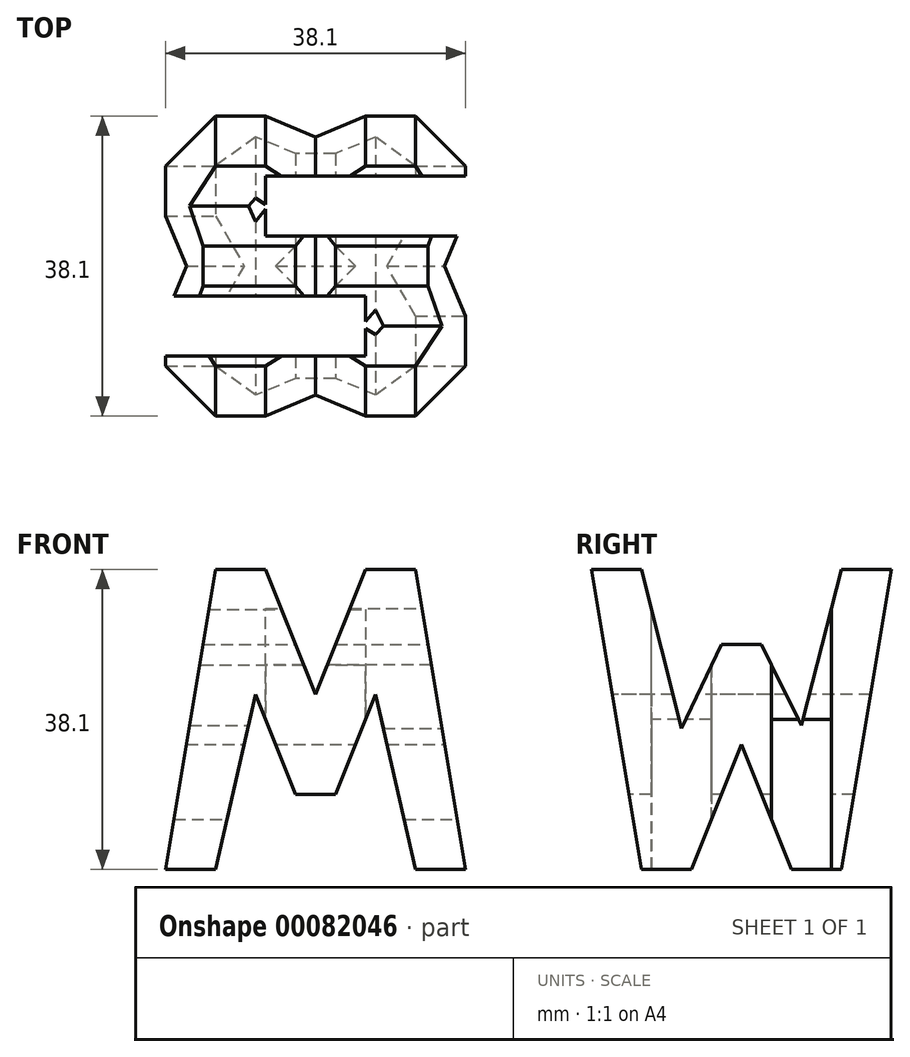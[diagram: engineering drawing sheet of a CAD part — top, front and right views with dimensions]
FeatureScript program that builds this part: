
annotation { "Feature Type Name" : "Feature", "Feature Type Description" : "" }
export const myFeature = defineFeature(function(context is Context, id is Id, definition is map)
    precondition{}
    {
        {
            var Q0;
            Q0=qCreatedBy(makeId("Front.planeOp"),FACE);
            var sketch = newSketch(context, id + "F0", { "sketchPlane" : qUnion([Q0])});
            skLineSegment(sketch, "E0", {"start": v(0, 0) * mm, "end": v(0, 38.1) * mm});
            skLineSegment(sketch, "E1", {"start": v(0, 38.1) * mm, "end": v(38.1, 38.1) * mm});
            skLineSegment(sketch, "E2", {"start": v(38.1, 38.1) * mm, "end": v(38.1, 0) * mm});
            skLineSegment(sketch, "E3", {"start": v(38.1, 0) * mm, "end": v(0, 0) * mm});
            skSolve(sketch);
        }
        {
            var Q0;
            Q0=makeQuery(id+"F0.imprint","IMPRINT",FACE,{"disambiguationData":[TD([[makeQuery(id+"F0.imprint","IMPRINT",EDGE,{"derivedFrom":sQuery(id+"F0.wireOp",EDGE,"E0")}),-1.0]])]});
            extrude(context, id + "F1", {"entities" : qUnion([Q0]), "depth" : 38.1 * mm});
        }
        {
            var Q0;
            Q0=qCreatedBy(makeId("Front.planeOp"),FACE);
            cPlane(context, id + "F2", {"entities" : qUnion([Q0]), "cplaneType" : CPlaneType.OFFSET, "offset" : 38.1 * mm, "width" : 152.4 * mm, "height" : 152.4 * mm});
        }
        {
            var Q0;
            Q0=qCreatedBy(makeId("Right.planeOp"),FACE);
            cPlane(context, id + "F3", {"entities" : qUnion([Q0]), "cplaneType" : CPlaneType.OFFSET, "offset" : 38.1 * mm, "width" : 152.4 * mm, "height" : 152.4 * mm});
        }
        {
            var Q0;
            Q0=qCreatedBy(makeId("Top.planeOp"),FACE);
            cPlane(context, id + "F4", {"entities" : qUnion([Q0]), "cplaneType" : CPlaneType.OFFSET, "offset" : 38.1 * mm, "width" : 152.4 * mm, "height" : 152.4 * mm});
        }
        {
            var Q0;
            Q0=qCreatedBy(id+"F3.planeOp",FACE);
            var sketch = newSketch(context, id + "F5", { "sketchPlane" : qUnion([Q0])});
            skLineSegment(sketch, "E4", {"start": v(0, 0) * mm, "end": v(-38.1, 0) * mm});
            skLineSegment(sketch, "E5", {"start": v(-38.1, 0) * mm, "end": v(-38.1, 38.1) * mm});
            skLineSegment(sketch, "E6", {"start": v(-38.1, 38.1) * mm, "end": v(0, 38.1) * mm});
            skLineSegment(sketch, "E7", {"start": v(0, 38.1) * mm, "end": v(0, 0) * mm});
            skLineSegment(sketch, "E8", {"start": v(-38.1, 38.1) * mm, "end": v(-31.75, 0) * mm});
            skLineSegment(sketch, "E9", {"start": v(-31.75, 38.1) * mm, "end": v(-26.67, 17.88) * mm});
            skLineSegment(sketch, "E10", {"start": v(-26.67, 17.88) * mm, "end": v(-21.59, 28.58) * mm});
            skLineSegment(sketch, "E11", {"start": v(-21.6, 28.58) * mm, "end": v(-16.51, 28.58) * mm});
            skLineSegment(sketch, "E12", {"start": v(-16.51, 28.58) * mm, "end": v(-11.43, 18.3) * mm});
            skLineSegment(sketch, "E13", {"start": v(-11.43, 18.3) * mm, "end": v(-6.35, 38.1) * mm});
            skLineSegment(sketch, "E14", {"start": v(-6.35, 38.1) * mm, "end": v(0, 38.1) * mm});
            skLineSegment(sketch, "E15", {"start": v(0, 38.1) * mm, "end": v(-6.35, 0) * mm});
            skLineSegment(sketch, "E16", {"start": v(-12.7, 0) * mm, "end": v(-19.05, 15.88) * mm});
            skLineSegment(sketch, "E17", {"start": v(-19.05, 15.88) * mm, "end": v(-25.4, 0) * mm});
            skSolve(sketch);
        }
        {
            var Q0;
            {var subQ0=sQuery(id+"F5.wireOp",EDGE,"E9");Q0=makeQuery(id+"F5.imprint","IMPRINT",FACE,{"disambiguationData":[TD([[makeQuery(id+"F5.imprint","IMPRINT",EDGE,{"derivedFrom":subQ0}),1.0]])]});}
            var Q1;
            {var subQ0=sQuery(id+"F5.wireOp",EDGE,"E5");Q1=makeQuery(id+"F5.imprint","IMPRINT",FACE,{"disambiguationData":[TD([[makeQuery(id+"F5.imprint","IMPRINT",EDGE,{"derivedFrom":subQ0}),-1.0]])]});}
            var Q2;
            {var subQ0=sQuery(id+"F5.wireOp",EDGE,"E16");Q2=makeQuery(id+"F5.imprint","IMPRINT",FACE,{"disambiguationData":[TD([[makeQuery(id+"F5.imprint","IMPRINT",EDGE,{"derivedFrom":subQ0}),1.0]])]});}
            var Q3;
            {var subQ0=sQuery(id+"F5.wireOp",EDGE,"E7");Q3=makeQuery(id+"F5.imprint","IMPRINT",FACE,{"disambiguationData":[TD([[makeQuery(id+"F5.imprint","IMPRINT",EDGE,{"derivedFrom":subQ0}),-1.0]])]});}
            extrude(context, id + "F6", {"entities" : qUnion([Q0, Q1, Q2, Q3]), "operationType" : NewBodyOperationType.REMOVE, "oppositeDirection" : true, "depth" : 38.1 * mm});
        }
        {
            var Q0;
            Q0=qCreatedBy(id+"F2.planeOp",FACE);
            var sketch = newSketch(context, id + "F7", { "sketchPlane" : qUnion([Q0])});
            skLineSegment(sketch, "E18", {"start": v(0, 0) * mm, "end": v(0, 38.1) * mm});
            skLineSegment(sketch, "E19", {"start": v(0, 38.1) * mm, "end": v(38.1, 38.1) * mm});
            skLineSegment(sketch, "E20", {"start": v(38.1, 38.1) * mm, "end": v(38.1, 0) * mm});
            skLineSegment(sketch, "E21", {"start": v(38.1, 0) * mm, "end": v(0, 0) * mm});
            skLineSegment(sketch, "E22", {"start": v(0, 0) * mm, "end": v(6.35, 38.1) * mm});
            skLineSegment(sketch, "E23", {"start": v(12.7, 38.1) * mm, "end": v(19.05, 22.22) * mm});
            skLineSegment(sketch, "E24", {"start": v(19.05, 22.22) * mm, "end": v(25.4, 38.1) * mm});
            skLineSegment(sketch, "E25", {"start": v(31.75, 38.1) * mm, "end": v(38.1, 0) * mm});
            skLineSegment(sketch, "E26", {"start": v(38.1, 0) * mm, "end": v(31.75, 0) * mm});
            skLineSegment(sketch, "E27", {"start": v(31.75, 0) * mm, "end": v(26.67, 22.22) * mm});
            skLineSegment(sketch, "E28", {"start": v(26.67, 22.22) * mm, "end": v(21.6, 9.53) * mm});
            skLineSegment(sketch, "E29", {"start": v(21.59, 9.52) * mm, "end": v(16.51, 9.52) * mm});
            skLineSegment(sketch, "E30", {"start": v(16.51, 9.52) * mm, "end": v(11.43, 22.23) * mm});
            skLineSegment(sketch, "E31", {"start": v(11.43, 22.23) * mm, "end": v(6.35, 0) * mm});
            skSolve(sketch);
        }
        {
            var Q0;
            {var subQ0=sQuery(id+"F7.wireOp",EDGE,"E23");Q0=makeQuery(id+"F7.imprint","IMPRINT",FACE,{"disambiguationData":[TD([[makeQuery(id+"F7.imprint","IMPRINT",EDGE,{"derivedFrom":subQ0}),1.0]])]});}
            var sketch = newSketch(context, id + "F8", { "sketchPlane" : qUnion([Q0])});
            skSolve(sketch);
        }
        {
            var Q0;
            Q0 = qSketchRegion(id + "F8", true);
            var Q1;
            {var subQ0=sQuery(id+"F7.wireOp",EDGE,"E23");Q1=makeQuery(id+"F7.imprint","IMPRINT",FACE,{"disambiguationData":[TD([[makeQuery(id+"F7.imprint","IMPRINT",EDGE,{"derivedFrom":subQ0}),1.0]])]});}
            var Q2;
            {var subQ0=sQuery(id+"F7.wireOp",EDGE,"E18");Q2=makeQuery(id+"F7.imprint","IMPRINT",FACE,{"disambiguationData":[TD([[makeQuery(id+"F7.imprint","IMPRINT",EDGE,{"derivedFrom":subQ0}),-1.0]])]});}
            var Q3;
            {var subQ0=sQuery(id+"F7.wireOp",EDGE,"E27");Q3=makeQuery(id+"F7.imprint","IMPRINT",FACE,{"disambiguationData":[TD([[makeQuery(id+"F7.imprint","IMPRINT",EDGE,{"derivedFrom":subQ0}),1.0]])]});}
            var Q4;
            {var subQ0=sQuery(id+"F7.wireOp",EDGE,"E20");Q4=makeQuery(id+"F7.imprint","IMPRINT",FACE,{"disambiguationData":[TD([[makeQuery(id+"F7.imprint","IMPRINT",EDGE,{"derivedFrom":subQ0}),-1.0]])]});}
            extrude(context, id + "F9", {"entities" : qUnion([Q0, Q1, Q2, Q3, Q4]), "operationType" : NewBodyOperationType.REMOVE, "oppositeDirection" : true, "depth" : 38.1 * mm});
        }
        {
            var Q0;
            Q0=qCreatedBy(id+"F4.planeOp",FACE);
            var sketch = newSketch(context, id + "F10", { "sketchPlane" : qUnion([Q0])});
            skLineSegment(sketch, "E32", {"start": v(0, 0) * mm, "end": v(0, -38.1) * mm});
            skLineSegment(sketch, "E33", {"start": v(0, -38.1) * mm, "end": v(38.1, -38.1) * mm});
            skLineSegment(sketch, "E34", {"start": v(38.1, -38.1) * mm, "end": v(38.1, 0) * mm});
            skLineSegment(sketch, "E35", {"start": v(38.1, 0) * mm, "end": v(0, 0) * mm});
            skLineSegment(sketch, "E36", {"start": v(38.1, -7.62) * mm, "end": v(12.7, -7.62) * mm});
            skLineSegment(sketch, "E37", {"start": v(12.7, -7.62) * mm, "end": v(12.7, -15.24) * mm});
            skLineSegment(sketch, "E38", {"start": v(12.7, -15.24) * mm, "end": v(38.1, -15.24) * mm});
            skLineSegment(sketch, "E39", {"start": v(0, -22.86) * mm, "end": v(25.4, -22.86) * mm});
            skLineSegment(sketch, "E40", {"start": v(25.4, -22.86) * mm, "end": v(25.4, -30.48) * mm});
            skLineSegment(sketch, "E41", {"start": v(25.4, -30.48) * mm, "end": v(0, -30.48) * mm});
            skSolve(sketch);
        }
        {
            var Q0;
            {var subQ6=sQuery(id+"F10.wireOp",EDGE,"E33");Q0=makeQuery(id+"F10.imprint","IMPRINT",FACE,{"disambiguationData":[TD([[makeQuery(id+"F10.imprint","IMPRINT",EDGE,{"derivedFrom":subQ6}),1.0]])]});}
            var sketch = newSketch(context, id + "F11", { "sketchPlane" : qUnion([Q0])});
            skSolve(sketch);
        }
        {
            var Q0;
            Q0 = qSketchRegion(id + "F11", true);
            var Q1;
            {var subQ0=sQuery(id+"F10.wireOp",EDGE,"E36");Q1=makeQuery(id+"F10.imprint","IMPRINT",FACE,{"disambiguationData":[TD([[makeQuery(id+"F10.imprint","IMPRINT",EDGE,{"derivedFrom":subQ0}),1.0]])]});}
            var Q2;
            {var subQ0=sQuery(id+"F10.wireOp",EDGE,"E39");Q2=makeQuery(id+"F10.imprint","IMPRINT",FACE,{"disambiguationData":[TD([[makeQuery(id+"F10.imprint","IMPRINT",EDGE,{"derivedFrom":subQ0}),-1.0]])]});}
            extrude(context, id + "F12", {"entities" : qUnion([Q0, Q1, Q2]), "operationType" : NewBodyOperationType.REMOVE, "oppositeDirection" : true, "depth" : 38.1 * mm});
        }
    });
